# Revit family: Очаг Cassette 1000 PS RETAIL LOGSET
name_source: partatom
category: Оборудование
units: mm (PartAtom-declared; Revit-internal decimal feet)

## family parameters
Всегда вертикально = Нет
Классификация = Нет
На основе рабочей плоскости = Да
Общий = Нет
При загрузке вырезать с полостями = Нет
Размер круглого соединителя = Использовать диаметр
Тип детали = Нормальный
Точка расчета площади = Нет

## types (1)
- Cassette 1000 PS RETAIL LOGSET
    ADSK_Версия Revit = 2019
    ADSK_Единица измерения = шт.
    ADSK_Завод-изготовитель = Dimplex
    ADSK_Классификация нагрузок = Прочее
    ADSK_Код изделия = нет данных
    ADSK_Количество = 1
    ADSK_Количество фаз = 1
    ADSK_Коэффициент мощности = 0
    ADSK_Масса = 34
    ADSK_Масса_Текст = 34
    ADSK_Наименование = Cassette 1000 PS RETAIL LOGSET
    ADSK_Наименование краткое = Электрический очаг
    ADSK_Напряжение = 230 В
    ADSK_Номинальная мощность = 0 Вт
    ADSK_Полная мощность = 0 В·А
    ADSK_Ток = 0 А
    Высота камина = 175 мм
    Высота ножек = 50 мм
    Габариты = 237 × 508 × 354
    Длина камина без планок = 1009 мм
    Длина камина с планками = 760 мм
    Изображение типоразмера = <Нет>
    Отметка по умолчанию = 1219 мм
    Разработчик = https://3dbim.pro
    Расстояние между ножками = 700 мм
    Ширина камина = 300 мм
